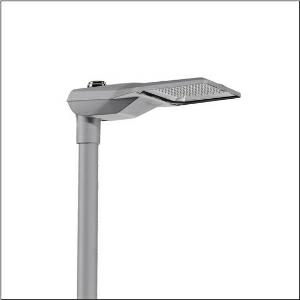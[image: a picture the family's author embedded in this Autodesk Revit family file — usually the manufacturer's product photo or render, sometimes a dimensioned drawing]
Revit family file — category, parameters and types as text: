
# Revit family: streetlight_sl_21_midi___st1_5a_5xe7p37n08lb_8b0d
name_source: partatom
category: Lighting Fixtures
units: mm (PartAtom-declared; Revit-internal decimal feet)

## family parameters
Cut with Voids When Loaded = No
Host = Face
Light Source = No
Part Type = Normal
Room Calculation Point = No
Round Connector Dimension = Use Diameter
Shared = No

## types (1)
- --- (1 x LED, 14100 lm, 98.3 W, 3000K)
    Apparent Load = 98 VA
    CIE Flux Codes = 22 53 95 100 100
    Color Rendering = 70
    Color Temperature = 3000K
    Default Elevation = 1800 mm
    Description = Streetlight SL 21 midi, mast luminaire, primary light control with lens, of PMMA, primary optical cover: cover, of toughened safety glass, transparent, light distribution: ST1.5a, light emission: direct distribution, primary light characteristic: asymmetric, installation type: side-entry, LED, 3G 2.5mm², High Power LED, rated luminous flux: 14.100lm, luminous efficacy: 143lm/W, light colour: 730, colour temperature: 3000K, control gear: NEMA (7pin), control: overheat protection, pre-setting: linear dimming characteristic, constant luminous flux control, time-dependent luminous flux control, flexible luminous flux parameterisation, mains connection: 220..240V, AC, 50/60Hz, connection cable pre-assembled, cable length: 10,5m, wiring characteristics: H05VV-F, start of lifetime: 98W, end of service life: 101W, reduction: 45W, luminaire housing, of diecast aluminium (EN AC-44300), powder-coated, Siteco® metallic grey (DB 702S), corrosivity category C5 mid according to DIN EN ISO 12944, multi-level sealing system, sealing non-destructively replaceable, inclination adjustable: 0°, 5°, 10°, 15°, length: 644mm, width: 335mm, height: 110mm, spigot size: 42mm (side-entry), mounting height: 4..8m, protection rating (complete): IP66, insulation class (complete): insulation class I (protective earthing), certification: CE, ENEC, ENEC+, VDE, impact resistance: IK10, permissible operating ambient temperature for outdoor applications: -40..+50°C, standard-compliant lighting for roads and squares, packaging unit: 1 piece

Light Distribution: ST1.5a
    Height = 111 mm
    Lamp = 1 x LED
    Lamp Light Flux = 14100 lm
    Lamp Power = 98.3 W
    Lamp count = 1
    Length = 644 mm
    Luminous efficacy = 143 lm/W
    Manufacturer = Siteco
    ModVariant = No
    Model = 5XE7P37N08LB
    Number of Poles = 1
    OnlyDefault = Yes
    Power Factor = 1
    Product Name = Streetlight SL 21 midi | ST1.5a
    Product group = mast luminaire | pylon top
    ProductGroupID = 6100
    Protection Class = Protection class I
    Protection Degree = IP 66
    RLX_Detail_Level = 1
    RLX_Emergency_Light_Flux = 0 lm
    RLX_Emergency_Type = 0
    RLX_Emergency_Type_DB = No
    RlxData = <blob elided: 30229 chars, md5=0f474a2d>
    Socket = socket
    Standby Power = 0 W
    System Light Flux = 14100 lm
    System Power = 98 W
    Type Comments = factory setting: luminous flux: 100 % | dim-lin: 254 | 1020 mA
    Type Image = l_1294377.jpg
    URL = http://relux.com
    VarID = @adj_154979
    Voltage = 0 V
    Weight = 0.00 kg
    Width = 336 mm

## geometry (parser evidence)
native form markers: Blend x4, Sweep x9
no freeform markers — native parametric forms only
